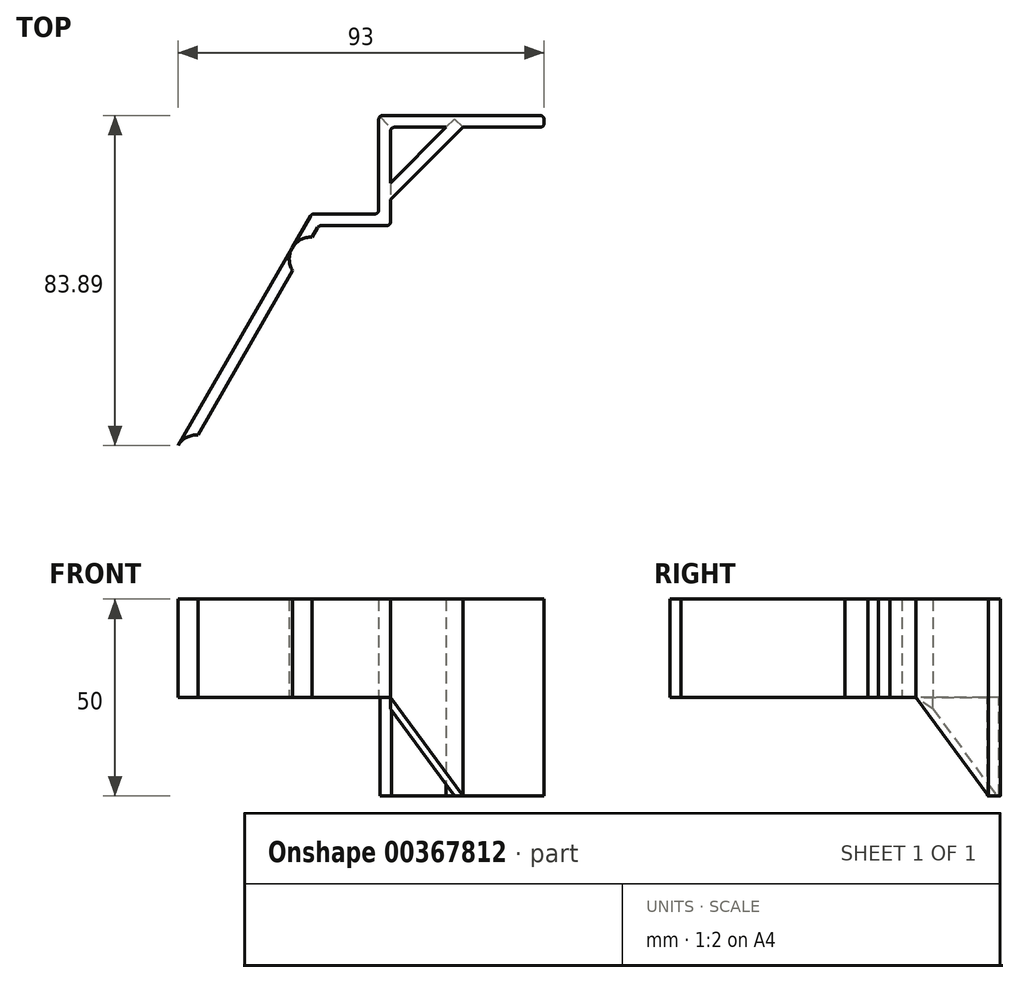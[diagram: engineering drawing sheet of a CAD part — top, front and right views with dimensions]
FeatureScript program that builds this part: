
annotation { "Feature Type Name" : "Feature", "Feature Type Description" : "" }
export const myFeature = defineFeature(function(context is Context, id is Id, definition is map)
    precondition{}
    {
        {
            var Q0;
            Q0=qCreatedBy(makeId("Top.planeOp"),FACE);
            var sketch = newSketch(context, id + "F0", { "sketchPlane" : qUnion([Q0])});
            skArc(sketch, "E0", {"start": v(0.22, -4.74) * mm, "mid": v(-4.11, 2.37) * mm, "end": v(4.22, 2.18) * mm});
            skLineSegment(sketch, "E1", {"start": v(0, 0) * mm, "end": v(29, 50.23) * mm, "construction": true});
            skArc(sketch, "E2", {"start": v(29.22, 45.48) * mm, "mid": v(24.89, 52.6) * mm, "end": v(33.22, 52.41) * mm});
            skArc(sketch, "E3.0.startCap", {"start": v(0.18, -4) * mm, "mid": v(0.97, -4.71) * mm, "end": v(0.25, -5.5) * mm});
            skArc(sketch, "E3.0.endCap", {"start": v(4.88, 2.53) * mm, "mid": v(4.56, 1.52) * mm, "end": v(3.55, 1.84) * mm});
            skArc(sketch, "E3.0.left", {"start": v(0.25, -5.5) * mm, "mid": v(-4.76, 2.75) * mm, "end": v(4.88, 2.53) * mm});
            skArc(sketch, "E3.0.right", {"start": v(0.18, -4) * mm, "mid": v(-3.46, 2) * mm, "end": v(3.55, 1.84) * mm});
            skArc(sketch, "E3.1.startCap", {"start": v(29.18, 46.23) * mm, "mid": v(29.97, 45.52) * mm, "end": v(29.25, 44.74) * mm});
            skArc(sketch, "E3.1.endCap", {"start": v(33.88, 52.76) * mm, "mid": v(33.56, 51.75) * mm, "end": v(32.55, 52.07) * mm});
            skArc(sketch, "E3.1.left", {"start": v(29.25, 44.74) * mm, "mid": v(24.24, 52.98) * mm, "end": v(33.88, 52.76) * mm});
            skArc(sketch, "E3.1.right", {"start": v(29.18, 46.23) * mm, "mid": v(25.54, 52.23) * mm, "end": v(32.55, 52.07) * mm});
            skLineSegment(sketch, "E4", {"start": v(-4.76, 2.75) * mm, "end": v(24.24, 52.98) * mm});
            skLineSegment(sketch, "E5", {"start": v(0.28, 5.5) * mm, "end": v(24.39, 47.24) * mm});
            skLineSegment(sketch, "E6", {"start": v(0.22, -4.74) * mm, "end": v(4.22, 2.18) * mm, "construction": true});
            skLineSegment(sketch, "E7", {"start": v(29.22, 45.48) * mm, "end": v(33.22, 52.41) * mm, "construction": true});
            skLineSegment(sketch, "E8", {"start": v(24.24, 52.98) * mm, "end": v(28.95, 61.14) * mm});
            skLineSegment(sketch, "E9", {"start": v(29.28, 55.72) * mm, "end": v(30.68, 58.14) * mm});
            skLineSegment(sketch, "E10", {"start": v(29.81, 61.64) * mm, "end": v(45.24, 61.64) * mm});
            skLineSegment(sketch, "E11", {"start": v(49.24, 61.64) * mm, "end": v(49.24, 59.64) * mm});
            skLineSegment(sketch, "E12", {"start": v(48.24, 58.64) * mm, "end": v(31.55, 58.64) * mm});
            skLineSegment(sketch, "E13", {"start": v(46.24, 62.64) * mm, "end": v(46.24, 85.64) * mm});
            skLineSegment(sketch, "E14", {"start": v(47.24, 86.64) * mm, "end": v(87.24, 86.64) * mm});
            skLineSegment(sketch, "E15", {"start": v(88.24, 85.64) * mm, "end": v(88.24, 84.64) * mm});
            skLineSegment(sketch, "E16", {"start": v(87.24, 83.64) * mm, "end": v(50.24, 83.64) * mm});
            skLineSegment(sketch, "E17", {"start": v(49.24, 82.64) * mm, "end": v(49.24, 61.64) * mm});
            skPoint(sketch, "E18.visualSharp", {"position": v(30.97, 58.64) * mm});
            skArc(sketch, "E18.filletArc", {"start": v(31.55, 58.64) * mm, "mid": v(31.05, 58.5) * mm, "end": v(30.68, 58.14) * mm});
            skPoint(sketch, "E19.visualSharp", {"position": v(46.24, 61.64) * mm});
            skArc(sketch, "E19.filletArc", {"start": v(45.24, 61.64) * mm, "mid": v(45.94, 61.93) * mm, "end": v(46.24, 62.64) * mm});
            skPoint(sketch, "E20.visualSharp", {"position": v(49.24, 58.64) * mm});
            skArc(sketch, "E20.filletArc", {"start": v(48.24, 58.64) * mm, "mid": v(48.94, 58.93) * mm, "end": v(49.24, 59.64) * mm});
            skPoint(sketch, "E21.visualSharp", {"position": v(46.24, 86.64) * mm});
            skArc(sketch, "E21.filletArc", {"start": v(47.24, 86.64) * mm, "mid": v(46.53, 86.35) * mm, "end": v(46.24, 85.64) * mm});
            skPoint(sketch, "E22.visualSharp", {"position": v(49.24, 83.64) * mm});
            skArc(sketch, "E22.filletArc", {"start": v(50.24, 83.64) * mm, "mid": v(49.53, 83.35) * mm, "end": v(49.24, 82.64) * mm});
            skPoint(sketch, "E23.visualSharp", {"position": v(88.24, 83.64) * mm});
            skArc(sketch, "E23.filletArc", {"start": v(87.24, 83.64) * mm, "mid": v(87.94, 83.93) * mm, "end": v(88.24, 84.64) * mm});
            skPoint(sketch, "E24.visualSharp", {"position": v(88.24, 86.64) * mm});
            skArc(sketch, "E24.filletArc", {"start": v(88.24, 85.64) * mm, "mid": v(87.94, 86.35) * mm, "end": v(87.24, 86.64) * mm});
            skPoint(sketch, "E25.visualSharp", {"position": v(29.24, 61.64) * mm});
            skArc(sketch, "E25.filletArc", {"start": v(29.81, 61.64) * mm, "mid": v(29.31, 61.5) * mm, "end": v(28.95, 61.14) * mm});
            skLineSegment(sketch, "E26", {"start": v(49.24, 69.5) * mm, "end": v(63.38, 83.64) * mm});
            skLineSegment(sketch, "E27", {"start": v(49.24, 65.25) * mm, "end": v(67.62, 83.64) * mm});
            skLineSegment(sketch, "E28", {"start": v(46.24, 86.64) * mm, "end": v(50.24, 82.64) * mm});
            skSolve(sketch);
        }
        {
            var Q0;
            {var subQ3=sQuery(id+"F0.wireOp",EDGE,"E3.0.startCap");Q0=makeQuery(id+"F0.imprint","IMPRINT",FACE,{"disambiguationData":[TD([[makeQuery(id+"F0.imprint","IMPRINT",EDGE,{"derivedFrom":subQ3}),-1.0]])]});}
            var Q1;
            {var subQ0=sQuery(id+"F0.wireOp",EDGE,"E4");Q1=makeQuery(id+"F0.imprint","IMPRINT",FACE,{"disambiguationData":[TD([[makeQuery(id+"F0.imprint","IMPRINT",EDGE,{"derivedFrom":subQ0}),-1.0]])]});}
            var Q2;
            {var subQ3=sQuery(id+"F0.wireOp",EDGE,"E3.1.startCap");Q2=makeQuery(id+"F0.imprint","IMPRINT",FACE,{"disambiguationData":[TD([[makeQuery(id+"F0.imprint","IMPRINT",EDGE,{"derivedFrom":subQ3}),-1.0]])]});}
            var Q3;
            {var subQ1=sQuery(id+"F0.wireOp",EDGE,"E8");Q3=makeQuery(id+"F0.imprint","IMPRINT",FACE,{"disambiguationData":[TD([[makeQuery(id+"F0.imprint","IMPRINT",EDGE,{"derivedFrom":subQ1}),-1.0]])]});}
            var Q4;
            {var subQ0=sQuery(id+"F0.wireOp",EDGE,"E26");Q4=makeQuery(id+"F0.imprint","IMPRINT",FACE,{"disambiguationData":[TD([[makeQuery(id+"F0.imprint","IMPRINT",EDGE,{"derivedFrom":subQ0}),-1.0]])]});}
            var Q5;
            {var subQ8=sQuery(id+"F0.wireOp",EDGE,"E14");Q5=makeQuery(id+"F0.imprint","IMPRINT",FACE,{"disambiguationData":[TD([[makeQuery(id+"F0.imprint","IMPRINT",EDGE,{"derivedFrom":subQ8}),-1.0]])]});}
            extrude(context, id + "F1", {"entities" : qUnion([Q0, Q1, Q2, Q3, Q4, Q5]), "depth" : 25 * mm});
        }
        {
            var Q0;
            {var subQ8=sQuery(id+"F0.wireOp",EDGE,"E14");Q0=makeQuery(id+"F0.imprint","IMPRINT",FACE,{"disambiguationData":[TD([[makeQuery(id+"F0.imprint","IMPRINT",EDGE,{"derivedFrom":subQ8}),-1.0]])]});}
            var Q1;
            {var subQ0=sQuery(id+"F0.wireOp",EDGE,"E26");Q1=makeQuery(id+"F0.imprint","IMPRINT",FACE,{"disambiguationData":[TD([[makeQuery(id+"F0.imprint","IMPRINT",EDGE,{"derivedFrom":subQ0}),-1.0]])]});}
            extrude(context, id + "F2", {"entities" : qUnion([Q0, Q1]), "operationType" : NewBodyOperationType.ADD, "oppositeDirection" : true, "depth" : 25 * mm});
        }
        {
            var Q0;
            {var subQ0=sQuery(id+"F0.wireOp",EDGE,"E27");Q0=makeQuery(id+"F2.boolean.opBoolean","MERGE",FACE,{"derivedFrom":[makeQuery(id+"F1.opExtrude","SWEPT_FACE",FACE,{"disambiguationData":[OSD([subQ0])]}),makeQuery(id+"F2.opExtrude","SWEPT_FACE",FACE,{"disambiguationData":[OSD([subQ0])]})]});}
            var sketch = newSketch(context, id + "F3", { "sketchPlane" : qUnion([Q0])});
            skLineSegment(sketch, "E29", {"start": v(80.96, 0) * mm, "end": v(106.96, -25) * mm});
            skSolve(sketch);
        }
        {
            var Q0;
            Q0=makeQuery(id+"F3.imprint","IMPRINT",FACE,{"disambiguationData":[TD([[makeQuery(id+"F3.imprint","IMPRINT",EDGE,{"derivedFrom":sQuery(id+"F3.wireOp",EDGE,"E29")}),-1.0]])]});
            var Q1;
            {var subQ0=sQuery(id+"F0.wireOp",EDGE,"E26");Q1=makeQuery(id+"F2.boolean.opBoolean","MERGE",FACE,{"derivedFrom":[makeQuery(id+"F1.opExtrude","SWEPT_FACE",FACE,{"disambiguationData":[OSD([subQ0])]}),makeQuery(id+"F2.opExtrude","SWEPT_FACE",FACE,{"disambiguationData":[OSD([subQ0])]})]});}
            extrude(context, id + "F4", {"entities" : qUnion([Q0]), "operationType" : NewBodyOperationType.REMOVE, "endBound" : BoundingType.UP_TO_SURFACE, "oppositeDirection" : true, "endBoundEntityFace" : qUnion([Q1]), "depth" : 25 * mm});
        }
    });
